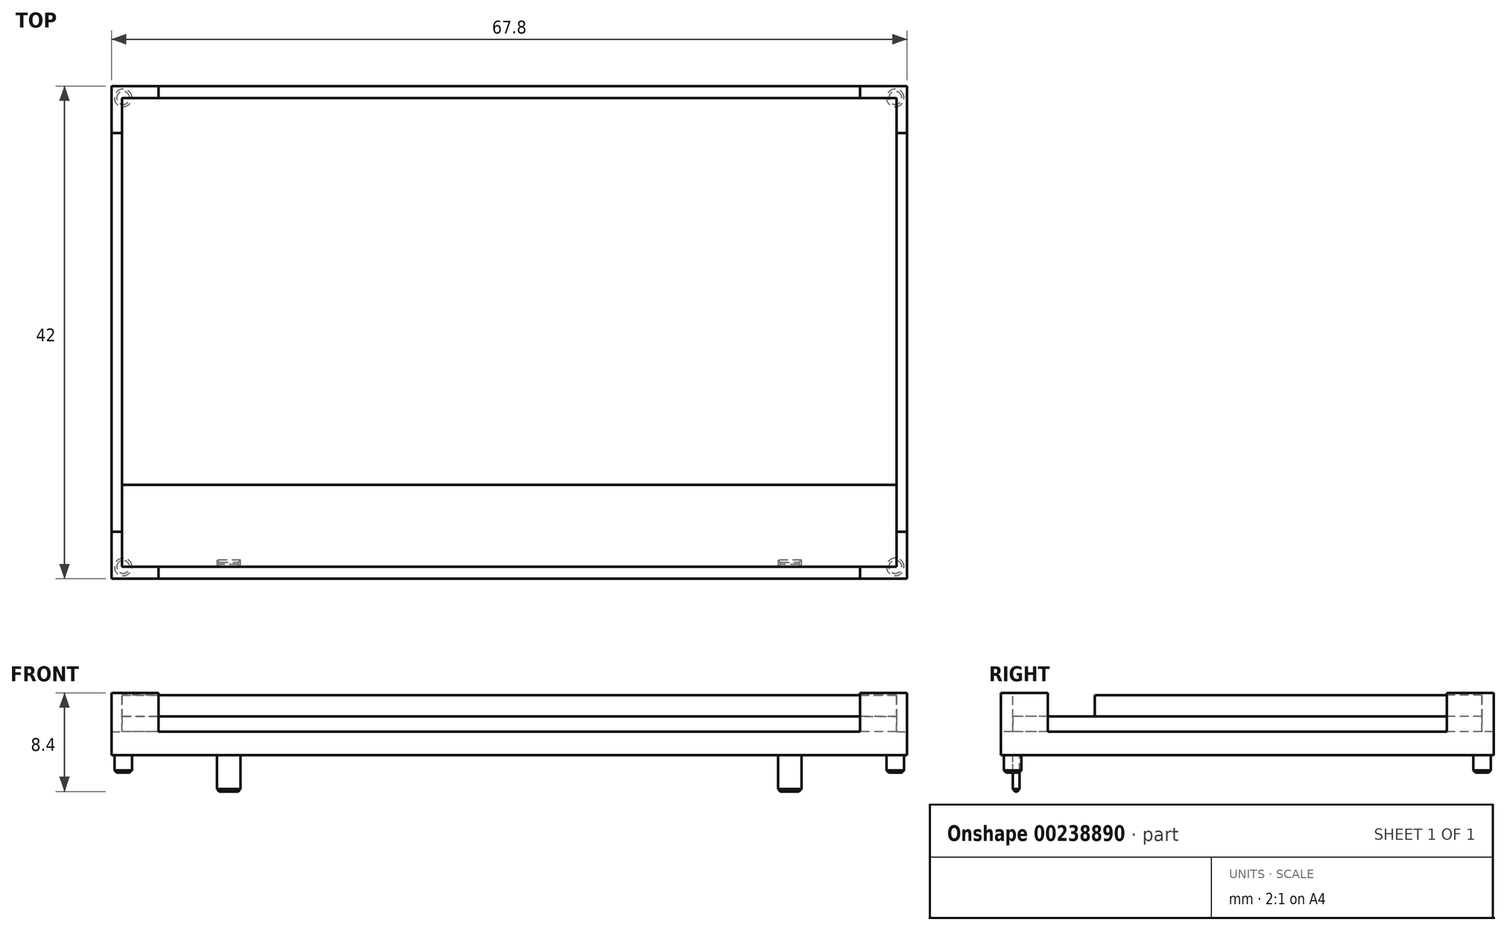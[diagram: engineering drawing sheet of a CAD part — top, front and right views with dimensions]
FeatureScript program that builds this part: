
annotation { "Feature Type Name" : "Feature", "Feature Type Description" : "" }
export const myFeature = defineFeature(function(context is Context, id is Id, definition is map)
    precondition{}
    {
        {
            var Q0;
            Q0=qCreatedBy(makeId("Top.planeOp"),FACE);
            var sketch = newSketch(context, id + "F0", { "sketchPlane" : qUnion([Q0])});
            skLineSegment(sketch, "E0.bottom", {"start": v(33.9, 21) * mm, "end": v(-33.9, 21) * mm});
            skLineSegment(sketch, "E0.top", {"start": v(33.9, -21) * mm, "end": v(-33.9, -21) * mm});
            skLineSegment(sketch, "E0.left", {"start": v(33.9, 21) * mm, "end": v(33.9, -21) * mm});
            skLineSegment(sketch, "E0.right", {"start": v(-33.9, 21) * mm, "end": v(-33.9, -21) * mm});
            skPoint(sketch, "E0.middle", {"position": v(0, 0) * mm});
            skCircle(sketch, "E1", {"center": v(-32.9, 20) * mm, "radius": 0.75 * mm});
            skCircle(sketch, "E2", {"center": v(32.9, 20) * mm, "radius": 0.75 * mm});
            skCircle(sketch, "E3", {"center": v(32.9, -20) * mm, "radius": 0.75 * mm});
            skCircle(sketch, "E4", {"center": v(-32.9, -20) * mm, "radius": 0.75 * mm});
            skLineSegment(sketch, "E5.bottom", {"start": v(-22.9, -20) * mm, "end": v(-24.9, -20) * mm});
            skLineSegment(sketch, "E5.top", {"start": v(-22.9, -19.4) * mm, "end": v(-24.9, -19.4) * mm});
            skLineSegment(sketch, "E5.left", {"start": v(-22.9, -20) * mm, "end": v(-22.9, -19.4) * mm});
            skLineSegment(sketch, "E5.right", {"start": v(-24.9, -20) * mm, "end": v(-24.9, -19.4) * mm});
            skPoint(sketch, "E5.middle", {"position": v(-23.9, -19.7) * mm});
            skLineSegment(sketch, "E6.bottom", {"start": v(24.9, -20) * mm, "end": v(22.9, -20) * mm});
            skLineSegment(sketch, "E6.top", {"start": v(24.9, -19.4) * mm, "end": v(22.9, -19.4) * mm});
            skLineSegment(sketch, "E6.left", {"start": v(24.9, -20) * mm, "end": v(24.9, -19.4) * mm});
            skLineSegment(sketch, "E6.right", {"start": v(22.9, -20) * mm, "end": v(22.9, -19.4) * mm});
            skPoint(sketch, "E6.middle", {"position": v(23.9, -19.7) * mm});
            skSolve(sketch);
        }
        {
            var Q0;
            Q0=makeQuery(id+"F0.imprint","IMPRINT",FACE,{"disambiguationData":[TD([[makeQuery(id+"F0.imprint","IMPRINT",EDGE,{"derivedFrom":sQuery(id+"F0.wireOp",EDGE,"E0.bottom")}),1.0]])]});
            var Q1;
            Q1=makeQuery(id+"F0.imprint","IMPRINT",FACE,{"disambiguationData":[TD([[makeQuery(id+"F0.imprint","IMPRINT",EDGE,{"derivedFrom":sQuery(id+"F0.wireOp",EDGE,"E2")}),1.0]])]});
            var Q2;
            Q2=makeQuery(id+"F0.imprint","IMPRINT",FACE,{"disambiguationData":[TD([[makeQuery(id+"F0.imprint","IMPRINT",EDGE,{"derivedFrom":sQuery(id+"F0.wireOp",EDGE,"E3")}),1.0]])]});
            var Q3;
            Q3=makeQuery(id+"F0.imprint","IMPRINT",FACE,{"disambiguationData":[TD([[makeQuery(id+"F0.imprint","IMPRINT",EDGE,{"derivedFrom":sQuery(id+"F0.wireOp",EDGE,"E1")}),1.0]])]});
            var Q4;
            Q4=makeQuery(id+"F0.imprint","IMPRINT",FACE,{"disambiguationData":[TD([[makeQuery(id+"F0.imprint","IMPRINT",EDGE,{"derivedFrom":sQuery(id+"F0.wireOp",EDGE,"E4")}),1.0]])]});
            var Q5;
            Q5=makeQuery(id+"F0.imprint","IMPRINT",FACE,{"disambiguationData":[TD([[makeQuery(id+"F0.imprint","IMPRINT",EDGE,{"derivedFrom":sQuery(id+"F0.wireOp",EDGE,"E5.bottom")}),-1.0]])]});
            var Q6;
            Q6=makeQuery(id+"F0.imprint","IMPRINT",FACE,{"disambiguationData":[TD([[makeQuery(id+"F0.imprint","IMPRINT",EDGE,{"derivedFrom":sQuery(id+"F0.wireOp",EDGE,"E6.bottom")}),-1.0]])]});
            extrude(context, id + "F1", {"entities" : qUnion([Q0, Q1, Q2, Q3, Q4, Q5, Q6]), "depth" : 5.3 * mm});
        }
        {
            var Q0;
            Q0=makeQuery(id+"F0.imprint","IMPRINT",FACE,{"disambiguationData":[TD([[makeQuery(id+"F0.imprint","IMPRINT",EDGE,{"derivedFrom":sQuery(id+"F0.wireOp",EDGE,"E4")}),1.0]])]});
            var Q1;
            Q1=makeQuery(id+"F0.imprint","IMPRINT",FACE,{"disambiguationData":[TD([[makeQuery(id+"F0.imprint","IMPRINT",EDGE,{"derivedFrom":sQuery(id+"F0.wireOp",EDGE,"E3")}),1.0]])]});
            var Q2;
            Q2=makeQuery(id+"F0.imprint","IMPRINT",FACE,{"disambiguationData":[TD([[makeQuery(id+"F0.imprint","IMPRINT",EDGE,{"derivedFrom":sQuery(id+"F0.wireOp",EDGE,"E2")}),1.0]])]});
            var Q3;
            Q3=makeQuery(id+"F0.imprint","IMPRINT",FACE,{"disambiguationData":[TD([[makeQuery(id+"F0.imprint","IMPRINT",EDGE,{"derivedFrom":sQuery(id+"F0.wireOp",EDGE,"E1")}),1.0]])]});
            extrude(context, id + "F2", {"entities" : qUnion([Q0, Q1, Q2, Q3]), "operationType" : NewBodyOperationType.ADD, "oppositeDirection" : true, "depth" : 1.5 * mm});
        }
        {
            var Q0;
            Q0=makeQuery(id+"F0.imprint","IMPRINT",FACE,{"disambiguationData":[TD([[makeQuery(id+"F0.imprint","IMPRINT",EDGE,{"derivedFrom":sQuery(id+"F0.wireOp",EDGE,"E5.bottom")}),-1.0]])]});
            var Q1;
            Q1=makeQuery(id+"F0.imprint","IMPRINT",FACE,{"disambiguationData":[TD([[makeQuery(id+"F0.imprint","IMPRINT",EDGE,{"derivedFrom":sQuery(id+"F0.wireOp",EDGE,"E6.bottom")}),-1.0]])]});
            extrude(context, id + "F3", {"entities" : qUnion([Q0, Q1]), "oppositeDirection" : true, "depth" : 3.1 * mm});
        }
        {
            var Q0;
            Q0=makeQuery(id+"F1.opExtrude","CAP_FACE",FACE,{"disambiguationData":[OSD([sQuery(id+"F0.wireOp",EDGE,"E0.bottom"),sQuery(id+"F0.wireOp",EDGE,"E0.top"),sQuery(id+"F0.wireOp",EDGE,"E0.left"),sQuery(id+"F0.wireOp",EDGE,"E0.right")])],"isStart":false});
            var sketch = newSketch(context, id + "F4", { "sketchPlane" : qUnion([Q0])});
            skLineSegment(sketch, "E7.bottom", {"start": v(33, 20) * mm, "end": v(29.9, 20) * mm});
            skLineSegment(sketch, "E7.top", {"start": v(33, -20) * mm, "end": v(29.9, -20) * mm});
            skLineSegment(sketch, "E7.left", {"start": v(33, 20) * mm, "end": v(33, 17) * mm});
            skLineSegment(sketch, "E7.right", {"start": v(-33, 20) * mm, "end": v(-33, 17) * mm});
            skPoint(sketch, "E7.middle", {"position": v(0, 0) * mm});
            skLineSegment(sketch, "E8", {"start": v(-33.9, 17) * mm, "end": v(-33, 17) * mm});
            skLineSegment(sketch, "E9", {"start": v(-29.9, 21) * mm, "end": v(-29.9, 20) * mm});
            skLineSegment(sketch, "E10", {"start": v(-33.9, -17) * mm, "end": v(-33, -17) * mm});
            skLineSegment(sketch, "E11", {"start": v(-29.9, -20) * mm, "end": v(-29.9, -21) * mm});
            skLineSegment(sketch, "E12", {"start": v(29.9, 21) * mm, "end": v(29.9, 20) * mm});
            skLineSegment(sketch, "E13", {"start": v(33, 17) * mm, "end": v(33.9, 17) * mm});
            skLineSegment(sketch, "E14", {"start": v(29.9, -20) * mm, "end": v(29.9, -21) * mm});
            skLineSegment(sketch, "E15", {"start": v(33, -17) * mm, "end": v(33.9, -17) * mm});
            skLineSegment(sketch, "E16", {"start": v(-33.9, 17) * mm, "end": v(-33.9, -17) * mm});
            skLineSegment(sketch, "E17", {"start": v(-29.9, -21) * mm, "end": v(29.9, -21) * mm});
            skLineSegment(sketch, "E18", {"start": v(33.9, -17) * mm, "end": v(33.9, 17) * mm});
            skLineSegment(sketch, "E19", {"start": v(29.9, 21) * mm, "end": v(-29.9, 21) * mm});
            skLineSegment(sketch, "E20.trimOffspring", {"start": v(-29.9, 20) * mm, "end": v(-33, 20) * mm});
            skLineSegment(sketch, "E21.trimOffspring", {"start": v(-33, -17) * mm, "end": v(-33, -20) * mm});
            skLineSegment(sketch, "E22.trimOffspring", {"start": v(-29.9, -20) * mm, "end": v(-33, -20) * mm});
            skLineSegment(sketch, "E23.trimOffspring", {"start": v(33, -17) * mm, "end": v(33, -20) * mm});
            skSolve(sketch);
        }
        {
            var Q0;
            Q0=makeQuery(id+"F4.imprint","IMPRINT",FACE,{"disambiguationData":[TD([[makeQuery(id+"F4.imprint","IMPRINT",EDGE,{"derivedFrom":sQuery(id+"F4.wireOp",EDGE,"E7.bottom")}),1.0]])]});
            extrude(context, id + "F5", {"entities" : qUnion([Q0]), "operationType" : NewBodyOperationType.REMOVE, "oppositeDirection" : true, "depth" : (5.3 - 2) * mm});
        }
        {
            var Q0;
            Q0=makeQuery(id+"F5.boolean.opBoolean","COPY",FACE,{"derivedFrom":makeQuery(id+"F5.opExtrude","CAP_FACE",FACE,{"disambiguationData":[OSD([sQuery(id+"F4.wireOp",EDGE,"E7.bottom"),sQuery(id+"F4.wireOp",EDGE,"E7.top"),sQuery(id+"F4.wireOp",EDGE,"E7.left"),sQuery(id+"F4.wireOp",EDGE,"E7.right"),sQuery(id+"F4.wireOp",EDGE,"E8"),sQuery(id+"F4.wireOp",EDGE,"E9"),sQuery(id+"F4.wireOp",EDGE,"E10"),sQuery(id+"F4.wireOp",EDGE,"E11"),sQuery(id+"F4.wireOp",EDGE,"E12"),sQuery(id+"F4.wireOp",EDGE,"E13"),sQuery(id+"F4.wireOp",EDGE,"E14"),sQuery(id+"F4.wireOp",EDGE,"E15"),sQuery(id+"F4.wireOp",EDGE,"E16"),sQuery(id+"F4.wireOp",EDGE,"E17"),sQuery(id+"F4.wireOp",EDGE,"E18"),sQuery(id+"F4.wireOp",EDGE,"E19"),sQuery(id+"F4.wireOp",EDGE,"E20.trimOffspring"),sQuery(id+"F4.wireOp",EDGE,"E21.trimOffspring"),sQuery(id+"F4.wireOp",EDGE,"E22.trimOffspring"),sQuery(id+"F4.wireOp",EDGE,"E23.trimOffspring")])],"isStart":false})});
            var sketch = newSketch(context, id + "F6", { "sketchPlane" : qUnion([Q0])});
            skLineSegment(sketch, "E24.bottom", {"start": v(33, 20) * mm, "end": v(-33, 20) * mm});
            skLineSegment(sketch, "E24.top", {"start": v(33, -20) * mm, "end": v(-33, -20) * mm});
            skLineSegment(sketch, "E24.left", {"start": v(33, 20) * mm, "end": v(33, -20) * mm});
            skLineSegment(sketch, "E24.right", {"start": v(-33, 20) * mm, "end": v(-33, -20) * mm});
            skPoint(sketch, "E24.middle", {"position": v(0, 0) * mm});
            skSolve(sketch);
        }
        {
            var Q0;
            {var subQ1=sQuery(id+"F6.wireOp",EDGE,"E24.bottom");var subQ13=makeQuery(id+"F6.imprint","INTERSECT",VERTEX,{"derivedFrom":[makeQuery(id+"F5.boolean.opBoolean","COPY",EDGE,{"derivedFrom":makeQuery(id+"F5.opExtrude","CAP_EDGE",EDGE,{"disambiguationData":[OSD([sQuery(id+"F4.wireOp",EDGE,"E12")])],"isStart":false})}),subQ1]});Q0=makeQuery(id+"F6.imprint","IMPRINT",FACE,{"disambiguationData":[TD([[makeQuery(id+"F6.imprint","IMPRINT",EDGE,{"disambiguationData":[TD([[subQ13,-1.0]])],"derivedFrom":subQ1}),1.0]])]});}
            extrude(context, id + "F7", {"entities" : qUnion([Q0]), "depth" : (5.3 - 2 - 2) * mm});
        }
        {
            var Q0;
            Q0=makeQuery(id+"F7.opExtrude","CAP_FACE",FACE,{"disambiguationData":[OSD([sQuery(id+"F6.wireOp",EDGE,"E24.bottom"),sQuery(id+"F6.wireOp",EDGE,"E24.top"),sQuery(id+"F6.wireOp",EDGE,"E24.left"),sQuery(id+"F6.wireOp",EDGE,"E24.right")])],"isStart":false});
            var sketch = newSketch(context, id + "F8", { "sketchPlane" : qUnion([Q0])});
            skLineSegment(sketch, "E25.bottom", {"start": v(-33, 20) * mm, "end": v(33, 20) * mm});
            skLineSegment(sketch, "E25.top", {"start": v(-33, -13) * mm, "end": v(33, -13) * mm});
            skLineSegment(sketch, "E25.left", {"start": v(-33, 20) * mm, "end": v(-33, -13) * mm});
            skLineSegment(sketch, "E25.right", {"start": v(33, 20) * mm, "end": v(33, -13) * mm});
            skSolve(sketch);
        }
        {
            var Q0;
            {var subQ0=sQuery(id+"F8.wireOp",EDGE,"E25.top");Q0=makeQuery(id+"F8.imprint","IMPRINT",FACE,{"disambiguationData":[TD([[makeQuery(id+"F8.imprint","IMPRINT",EDGE,{"derivedFrom":subQ0}),1.0]])]});}
            extrude(context, id + "F9", {"entities" : qUnion([Q0]), "depth" : (2 - 0.2) * mm});
        }
        {
            var Q0;
            Q0=makeQuery(id+"F2.opExtrude","CAP_EDGE",EDGE,{"disambiguationData":[OSD([sQuery(id+"F0.wireOp",EDGE,"E4")])],"isStart":false});
            var Q1;
            Q1=makeQuery(id+"F3.opExtrude","CAP_EDGE",EDGE,{"disambiguationData":[OSD([sQuery(id+"F0.wireOp",EDGE,"E5.bottom")])],"isStart":false});
            var Q2;
            Q2=makeQuery(id+"F3.opExtrude","CAP_EDGE",EDGE,{"disambiguationData":[OSD([sQuery(id+"F0.wireOp",EDGE,"E5.left")])],"isStart":false});
            var Q3;
            Q3=makeQuery(id+"F3.opExtrude","CAP_EDGE",EDGE,{"disambiguationData":[OSD([sQuery(id+"F0.wireOp",EDGE,"E5.top")])],"isStart":false});
            var Q4;
            Q4=makeQuery(id+"F3.opExtrude","CAP_EDGE",EDGE,{"disambiguationData":[OSD([sQuery(id+"F0.wireOp",EDGE,"E5.right")])],"isStart":false});
            var Q5;
            Q5=makeQuery(id+"F3.opExtrude","CAP_EDGE",EDGE,{"disambiguationData":[OSD([sQuery(id+"F0.wireOp",EDGE,"E6.top")])],"isStart":false});
            var Q6;
            Q6=makeQuery(id+"F3.opExtrude","CAP_EDGE",EDGE,{"disambiguationData":[OSD([sQuery(id+"F0.wireOp",EDGE,"E6.right")])],"isStart":false});
            var Q7;
            Q7=makeQuery(id+"F3.opExtrude","CAP_EDGE",EDGE,{"disambiguationData":[OSD([sQuery(id+"F0.wireOp",EDGE,"E6.bottom")])],"isStart":false});
            var Q8;
            Q8=makeQuery(id+"F3.opExtrude","CAP_EDGE",EDGE,{"disambiguationData":[OSD([sQuery(id+"F0.wireOp",EDGE,"E6.left")])],"isStart":false});
            var Q9;
            Q9=makeQuery(id+"F2.opExtrude","CAP_EDGE",EDGE,{"disambiguationData":[OSD([sQuery(id+"F0.wireOp",EDGE,"E3")])],"isStart":false});
            var Q10;
            Q10=makeQuery(id+"F2.opExtrude","CAP_EDGE",EDGE,{"disambiguationData":[OSD([sQuery(id+"F0.wireOp",EDGE,"E2")])],"isStart":false});
            var Q11;
            Q11=makeQuery(id+"F2.opExtrude","CAP_FACE",FACE,{"disambiguationData":[OSD([sQuery(id+"F0.wireOp",EDGE,"E1")])],"isStart":false});
            chamfer(context, id + "F10", {"entities" : qUnion([Q0, Q1, Q2, Q3, Q4, Q5, Q6, Q7, Q8, Q9, Q10, Q11]), "width" : 0.2 * mm, "tangentPropagation" : true});
        }
    });
